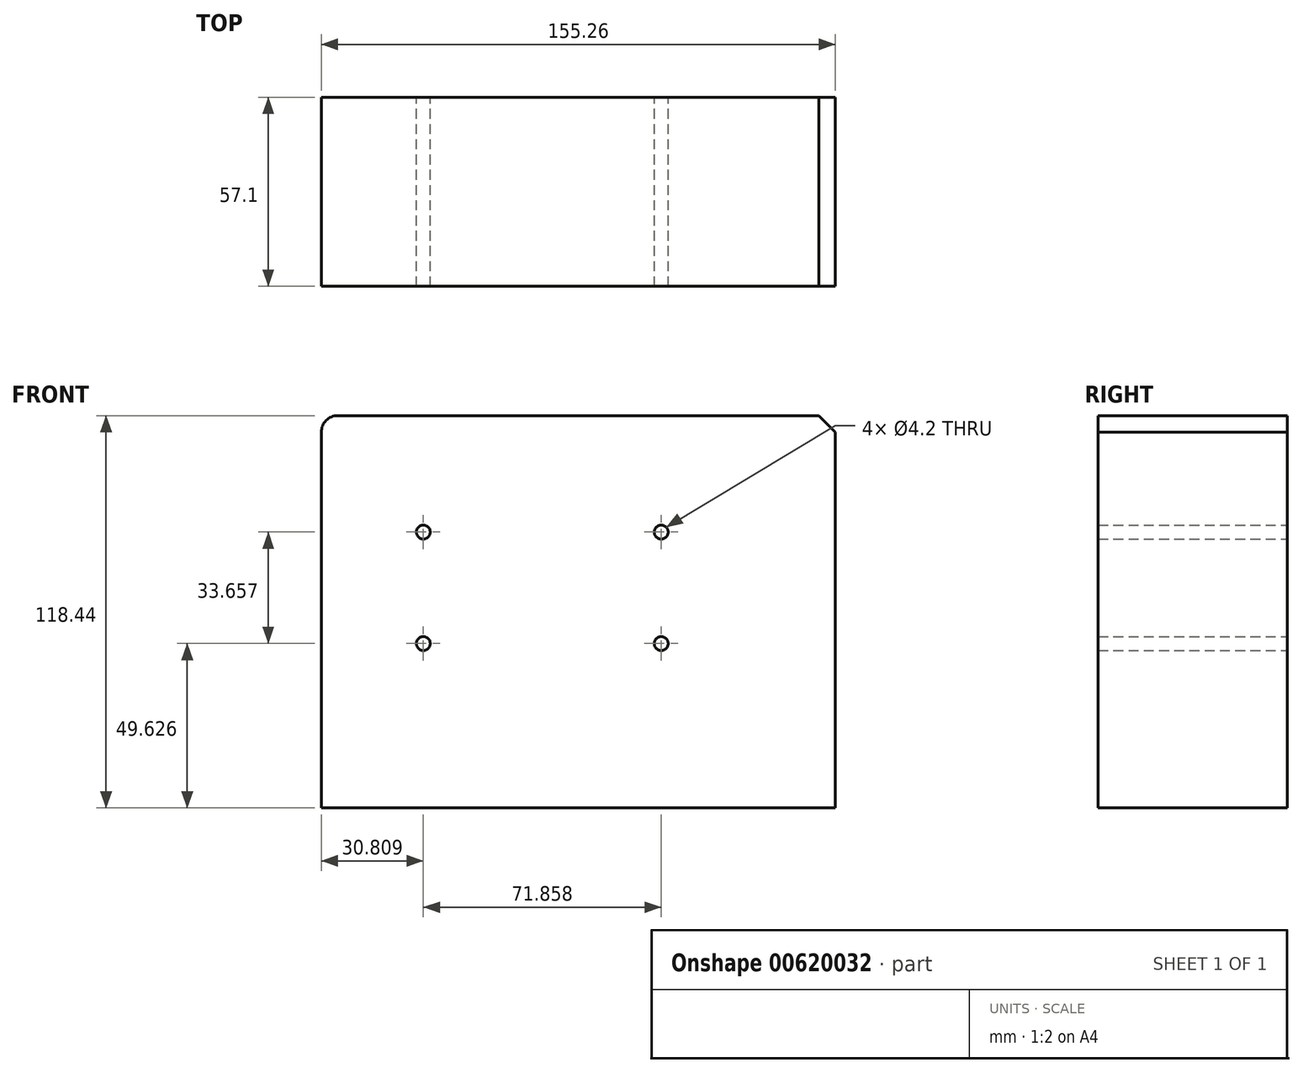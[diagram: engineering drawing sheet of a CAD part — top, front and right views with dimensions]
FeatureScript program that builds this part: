
annotation { "Feature Type Name" : "Feature", "Feature Type Description" : "" }
export const myFeature = defineFeature(function(context is Context, id is Id, definition is map)
    precondition{}
    {
        {
            var Q0;
            Q0=qCreatedBy(makeId("Front.planeOp"),FACE);
            var sketch = newSketch(context, id + "F0", { "sketchPlane" : qUnion([Q0])});
            skLineSegment(sketch, "E0.bottom", {"start": v(-67.24, -38.11) * mm, "end": v(88.02, -38.11) * mm});
            skLineSegment(sketch, "E0.top", {"start": v(-67.24, 80.33) * mm, "end": v(88.02, 80.33) * mm});
            skLineSegment(sketch, "E0.left", {"start": v(-67.24, -38.11) * mm, "end": v(-67.24, 80.33) * mm});
            skLineSegment(sketch, "E0.right", {"start": v(88.02, -38.11) * mm, "end": v(88.02, 80.33) * mm});
            skSolve(sketch);
        }
        {
            var Q0;
            Q0=makeQuery(id+"F0.imprint","IMPRINT",FACE,{"disambiguationData":[TD([[makeQuery(id+"F0.imprint","IMPRINT",EDGE,{"derivedFrom":sQuery(id+"F0.wireOp",EDGE,"E0.bottom")}),1.0]])]});
            extrude(context, id + "F1", {"entities" : qUnion([Q0]), "depth" : 57.1 * mm, "offsetDistance" : 25 * mm});
        }
        {
            var Q0;
            Q0=makeQuery(id+"F1.opExtrude","CAP_FACE",FACE,{"disambiguationData":[OSD([sQuery(id+"F0.wireOp",EDGE,"E0.bottom"),sQuery(id+"F0.wireOp",EDGE,"E0.top"),sQuery(id+"F0.wireOp",EDGE,"E0.left"),sQuery(id+"F0.wireOp",EDGE,"E0.right")])],"isStart":true});
            var sketch = newSketch(context, id + "F2", { "sketchPlane" : qUnion([Q0])});
            skPoint(sketch, "E1", {"position": v(-51.66, 59.46) * mm});
            skPoint(sketch, "E2", {"position": v(34.88, 55.91) * mm});
            skPoint(sketch, "E3", {"position": v(42.74, 4.38) * mm});
            skPoint(sketch, "E4", {"position": v(-55.7, 3.23) * mm});
            skLineSegment(sketch, "E5.bottom", {"start": v(-35.43, 45.17) * mm, "end": v(36.43, 45.17) * mm});
            skLineSegment(sketch, "E5.top", {"start": v(-35.43, 11.52) * mm, "end": v(36.43, 11.52) * mm});
            skLineSegment(sketch, "E5.left", {"start": v(-35.43, 45.17) * mm, "end": v(-35.43, 11.52) * mm});
            skLineSegment(sketch, "E5.right", {"start": v(36.43, 45.17) * mm, "end": v(36.43, 11.52) * mm});
            skSolve(sketch);
        }
        {
            var Q0;
            Q0=sQuery(id+"F2.wireOp",VERTEX,"E5.left.start");
            var Q1;
            Q1=sQuery(id+"F2.wireOp",VERTEX,"E5.right.start");
            var Q2;
            Q2=sQuery(id+"F2.wireOp",VERTEX,"E5.top.end");
            var Q3;
            Q3=sQuery(id+"F2.wireOp",VERTEX,"E5.left.end");
            var Q4;
            Q4=makeQuery(id+"F1.opExtrude","SWEPT_BODY",BODY,{"disambiguationData":[OSD([sQuery(id+"F0.wireOp",EDGE,"E0.bottom"),sQuery(id+"F0.wireOp",EDGE,"E0.top"),sQuery(id+"F0.wireOp",EDGE,"E0.left"),sQuery(id+"F0.wireOp",EDGE,"E0.right")])]});
            hole(context, id + "F3", {"style" : HoleStyle.SIMPLE, "endStyle" : HoleEndStyle.THROUGH, "standardTappedOrClearance" : lookupTablePath({ "standard" : "ISO", "engagement" : "75%", "pitch" : "0.8 mm", "size" : "M5", "type" : "Tapped" }), "standardBlindInLast" : lookupTablePath({ "standard" : "ISO", "engagement" : "75%", "pitch" : "0.8 mm", "size" : "M5", "type" : "Tapped" }), "holeDiameter" : 4.2 * mm, "majorDiameter" : 5 * mm, "showTappedDepth" : true, "isTappedThrough" : true, "tappedDepth" : 12 * mm, "tapClearance" : 3, "locations" : qUnion([Q0, Q1, Q2, Q3]), "scope" : qUnion([Q4])});
        }
        {
            var Q0;
            Q0=makeQuery(id+"F1.opExtrude","SWEPT_EDGE",EDGE,{"disambiguationData":[OSD([sQuery(id+"F0.wireOp",EDGE,"E0.top"),sQuery(id+"F0.wireOp",EDGE,"E0.left")])]});
            fillet(context, id + "F4", {"entities" : qUnion([Q0]), "radius" : 5 * mm, "tangentPropagation" : true, "allowEdgeOverflow" : false});
        }
        {
            var Q0;
            Q0=makeQuery(id+"F1.opExtrude","SWEPT_EDGE",EDGE,{"disambiguationData":[OSD([sQuery(id+"F0.wireOp",EDGE,"E0.top"),sQuery(id+"F0.wireOp",EDGE,"E0.right")])]});
            chamfer(context, id + "F5", {"entities" : qUnion([Q0]), "width" : 5 * mm, "tangentPropagation" : true});
        }
    });
